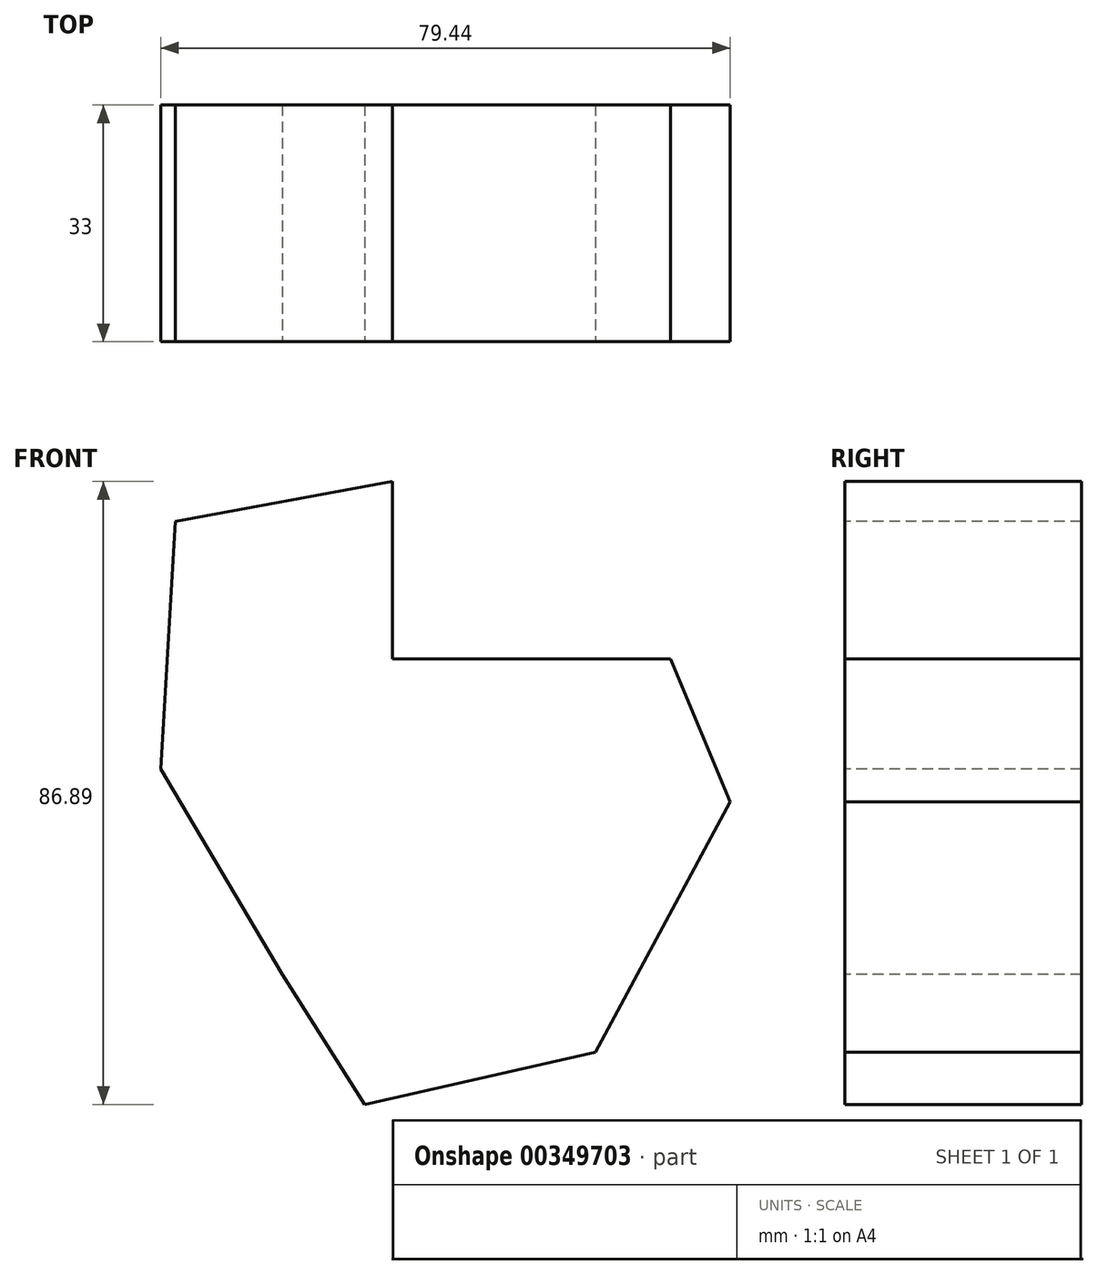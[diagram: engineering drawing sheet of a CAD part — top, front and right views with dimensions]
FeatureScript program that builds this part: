
annotation { "Feature Type Name" : "Feature", "Feature Type Description" : "" }
export const myFeature = defineFeature(function(context is Context, id is Id, definition is map)
    precondition{}
    {
        {
            var Q0;
            Q0=qCreatedBy(makeId("Front.planeOp"),FACE);
            var sketch = newSketch(context, id + "F0", { "sketchPlane" : qUnion([Q0])});
            skLineSegment(sketch, "E0", {"start": v(-28.29, 57.08) * mm, "end": v(-28.29, 32.35) * mm});
            skLineSegment(sketch, "E1", {"start": v(-28.29, 32.35) * mm, "end": v(10.5, 32.35) * mm});
            skLineSegment(sketch, "E2", {"start": v(10.5, 32.35) * mm, "end": v(18.8, 12.37) * mm});
            skLineSegment(sketch, "E3", {"start": v(18.8, 12.37) * mm, "end": v(0, -22.53) * mm});
            skLineSegment(sketch, "E4", {"start": v(0, -22.53) * mm, "end": v(-32.18, -29.81) * mm});
            skLineSegment(sketch, "E5", {"start": v(-32.18, -29.81) * mm, "end": v(-43.7, -11.69) * mm});
            skLineSegment(sketch, "E6", {"start": v(-43.7, -11.69) * mm, "end": v(-60.64, 16.94) * mm});
            skLineSegment(sketch, "E7", {"start": v(-60.64, 16.94) * mm, "end": v(-58.6, 51.5) * mm});
            skLineSegment(sketch, "E8", {"start": v(-58.6, 51.5) * mm, "end": v(-28.29, 57.08) * mm});
            skSolve(sketch);
        }
        {
            var Q0;
            Q0=makeQuery(id+"F0.imprint","IMPRINT",FACE,{"disambiguationData":[TD([[makeQuery(id+"F0.imprint","IMPRINT",EDGE,{"derivedFrom":sQuery(id+"F0.wireOp",EDGE,"E0")}),-1.0]])]});
            extrude(context, id + "F1", {"entities" : qUnion([Q0]), "oppositeDirection" : true, "depth" : 33 * mm});
        }
    });
